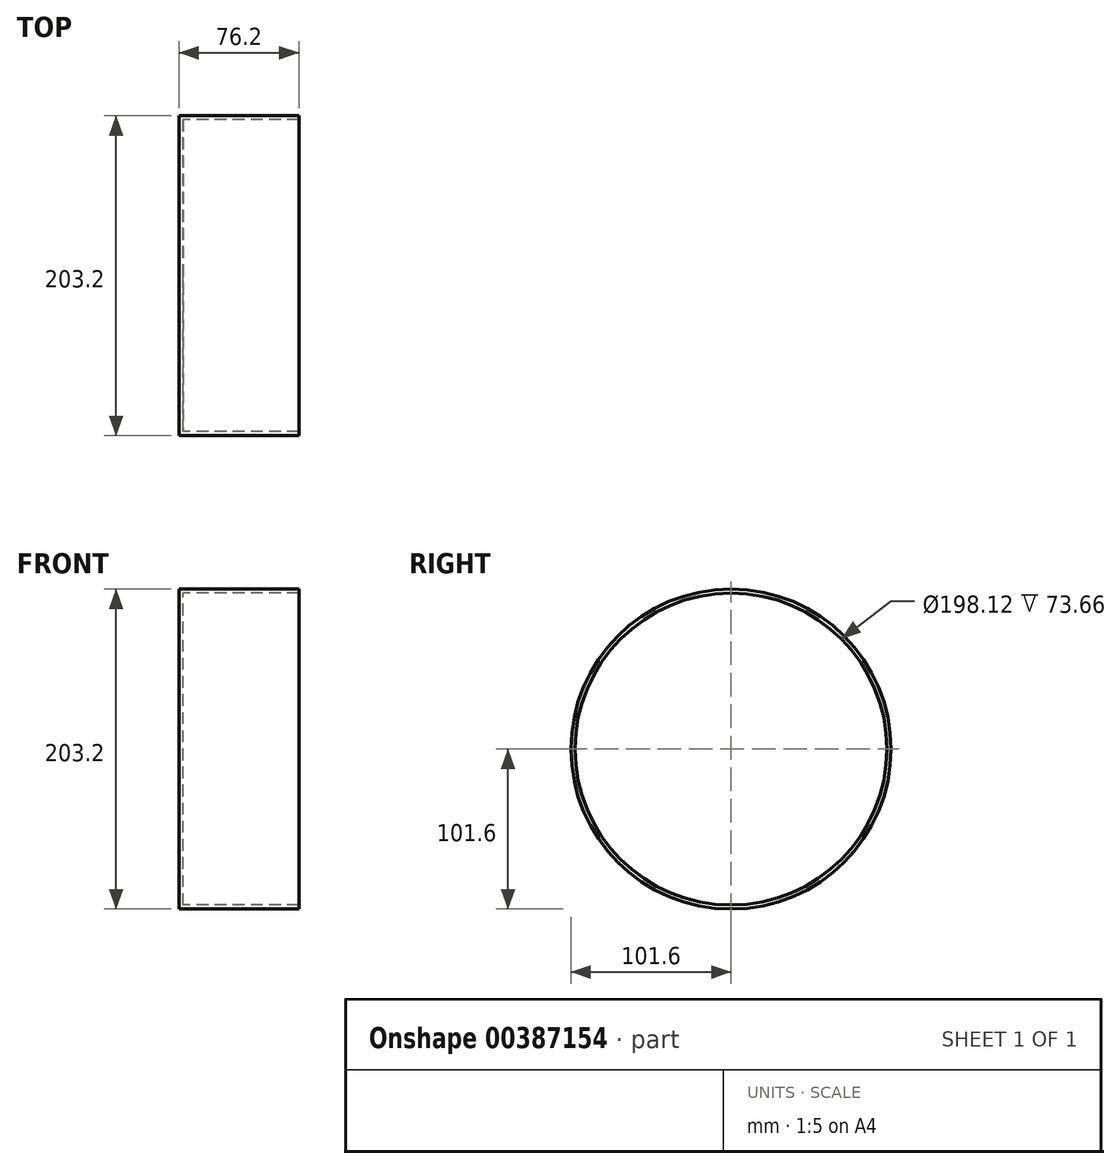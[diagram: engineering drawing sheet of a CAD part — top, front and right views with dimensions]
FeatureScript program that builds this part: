
annotation { "Feature Type Name" : "Feature", "Feature Type Description" : "" }
export const myFeature = defineFeature(function(context is Context, id is Id, definition is map)
    precondition{}
    {
        {
            var Q0;
            Q0=qCreatedBy(makeId("Right.planeOp"),FACE);
            var sketch = newSketch(context, id + "F0", { "sketchPlane" : qUnion([Q0])});
            skCircle(sketch, "E0", {"center": v(0, 0) * mm, "radius": 101.6 * mm});
            skSolve(sketch);
        }
        {
            var Q0;
            Q0 = qSketchRegion(id + "F0", true);
            extrude(context, id + "F1", {"entities" : qUnion([Q0]), "depth" : 76.2 * mm});
        }
        {
            var Q0;
            Q0=makeQuery(id+"F1.opExtrude","CAP_FACE",FACE,{"disambiguationData":[OSD([sQuery(id+"F0.wireOp",EDGE,"E0")])],"isStart":false});
            shell(context, id + "F2", {"entities" : qUnion([Q0]), "thickness" : 2.54 * mm});
        }
    });
